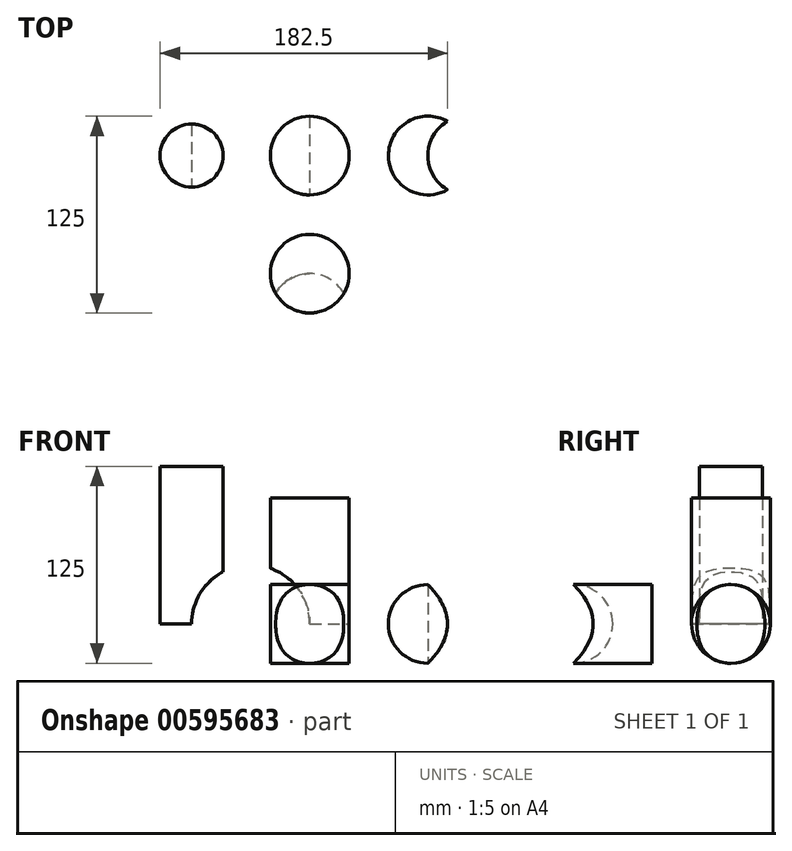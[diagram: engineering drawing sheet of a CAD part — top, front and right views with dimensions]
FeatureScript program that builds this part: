
annotation { "Feature Type Name" : "Feature", "Feature Type Description" : "" }
export const myFeature = defineFeature(function(context is Context, id is Id, definition is map)
    precondition{}
    {
        {
            var Q0;
            Q0=qCreatedBy(makeId("Top.planeOp"),FACE);
            var sketch = newSketch(context, id + "F0", { "sketchPlane" : qUnion([Q0])});
            skCircle(sketch, "E0", {"center": v(0, 0) * mm, "radius": 25 * mm});
            skSolve(sketch);
        }
        {
            var Q0;
            Q0 = qSketchRegion(id + "F0", true);
            extrude(context, id + "F1", {"entities" : qUnion([Q0]), "depth" : 80 * mm, "offsetDistance" : 25.4 * mm});
        }
        {
            var Q0;
            Q0=qCreatedBy(makeId("Top.planeOp"),FACE);
            var sketch = newSketch(context, id + "F2", { "sketchPlane" : qUnion([Q0])});
            skCircle(sketch, "E1", {"center": v(-75, 0) * mm, "radius": 20 * mm});
            skSolve(sketch);
        }
        {
            var Q0;
            Q0 = qSketchRegion(id + "F2", true);
            extrude(context, id + "F3", {"entities" : qUnion([Q0]), "depth" : 100 * mm, "offsetDistance" : 25 * mm});
        }
        {
            var Q0;
            Q0=qCreatedBy(makeId("Front.planeOp"),FACE);
            var sketch = newSketch(context, id + "F4", { "sketchPlane" : qUnion([Q0])});
            skCircle(sketch, "E2", {"center": v(-37.5, 0) * mm, "radius": 37.5 * mm});
            skSolve(sketch);
        }
        {
            var Q0;
            Q0 = qSketchRegion(id + "F4", true);
            extrude(context, id + "F5", {"entities" : qUnion([Q0]), "operationType" : NewBodyOperationType.REMOVE, "endBound" : BoundingType.SYMMETRIC, "oppositeDirection" : true, "depth" : 60 * mm, "offsetDistance" : 25 * mm});
        }
        {
            var Q0;
            Q0=qCreatedBy(makeId("Top.planeOp"),FACE);
            var sketch = newSketch(context, id + "F6", { "sketchPlane" : qUnion([Q0])});
            skArc(sketch, "E3", {"start": v(100, 0) * mm, "mid": v(75, 25) * mm, "end": v(50, 0) * mm});
            skLineSegment(sketch, "E4", {"start": v(50, 0) * mm, "end": v(100, 0) * mm});
            skPoint(sketch, "E5.orphan", {"position": v(43.48, 0) * mm});
            skSolve(sketch);
        }
        {
            var Q0;
            Q0 = qSketchRegion(id + "F6", true);
            var Q1;
            Q1=sQuery(id+"F6.wireOp",EDGE,"E4");
            revolve(context, id + "F7", {"entities" : qUnion([Q0]), "axis" : qUnion([Q1]), "revolveType" : RevolveType.ONE_DIRECTION, "angle" : 360 * degree});
        }
        {
            var Q0;
            Q0=qCreatedBy(makeId("Top.planeOp"),FACE);
            var sketch = newSketch(context, id + "F8", { "sketchPlane" : qUnion([Q0])});
            skCircle(sketch, "E6", {"center": v(100, 0) * mm, "radius": 25 * mm});
            skSolve(sketch);
        }
        {
            var Q0;
            Q0 = qSketchRegion(id + "F8", true);
            extrude(context, id + "F9", {"entities" : qUnion([Q0]), "operationType" : NewBodyOperationType.REMOVE, "endBound" : BoundingType.SYMMETRIC, "depth" : 100 * mm, "offsetDistance" : 25 * mm});
        }
        {
            var Q0;
            Q0=qCreatedBy(makeId("Top.planeOp"),FACE);
            var sketch = newSketch(context, id + "F10", { "sketchPlane" : qUnion([Q0])});
            skCircle(sketch, "E7", {"center": v(0, -75) * mm, "radius": 25 * mm});
            skSolve(sketch);
        }
        {
            var Q0;
            Q0 = qSketchRegion(id + "F10", true);
            extrude(context, id + "F11", {"entities" : qUnion([Q0]), "endBound" : BoundingType.SYMMETRIC, "depth" : 50 * mm, "offsetDistance" : 25 * mm});
        }
        {
            var Q0;
            Q0=qCreatedBy(makeId("Top.planeOp"),FACE);
            var sketch = newSketch(context, id + "F12", { "sketchPlane" : qUnion([Q0])});
            skArc(sketch, "E8", {"start": v(0, -125) * mm, "mid": v(25, -100) * mm, "end": v(0, -75) * mm});
            skLineSegment(sketch, "E9", {"start": v(0, -125) * mm, "end": v(0, -75) * mm});
            skPoint(sketch, "E10.orphan", {"position": v(0, -140.65) * mm});
            skSolve(sketch);
        }
        {
            var Q0;
            Q0 = qSketchRegion(id + "F12", true);
            var Q1;
            Q1=sQuery(id+"F12.wireOp",EDGE,"E9");
            revolve(context, id + "F13", {"operationType" : NewBodyOperationType.REMOVE, "entities" : qUnion([Q0]), "axis" : qUnion([Q1]), "revolveType" : RevolveType.FULL, "oppositeDirection" : true});
        }
    });
